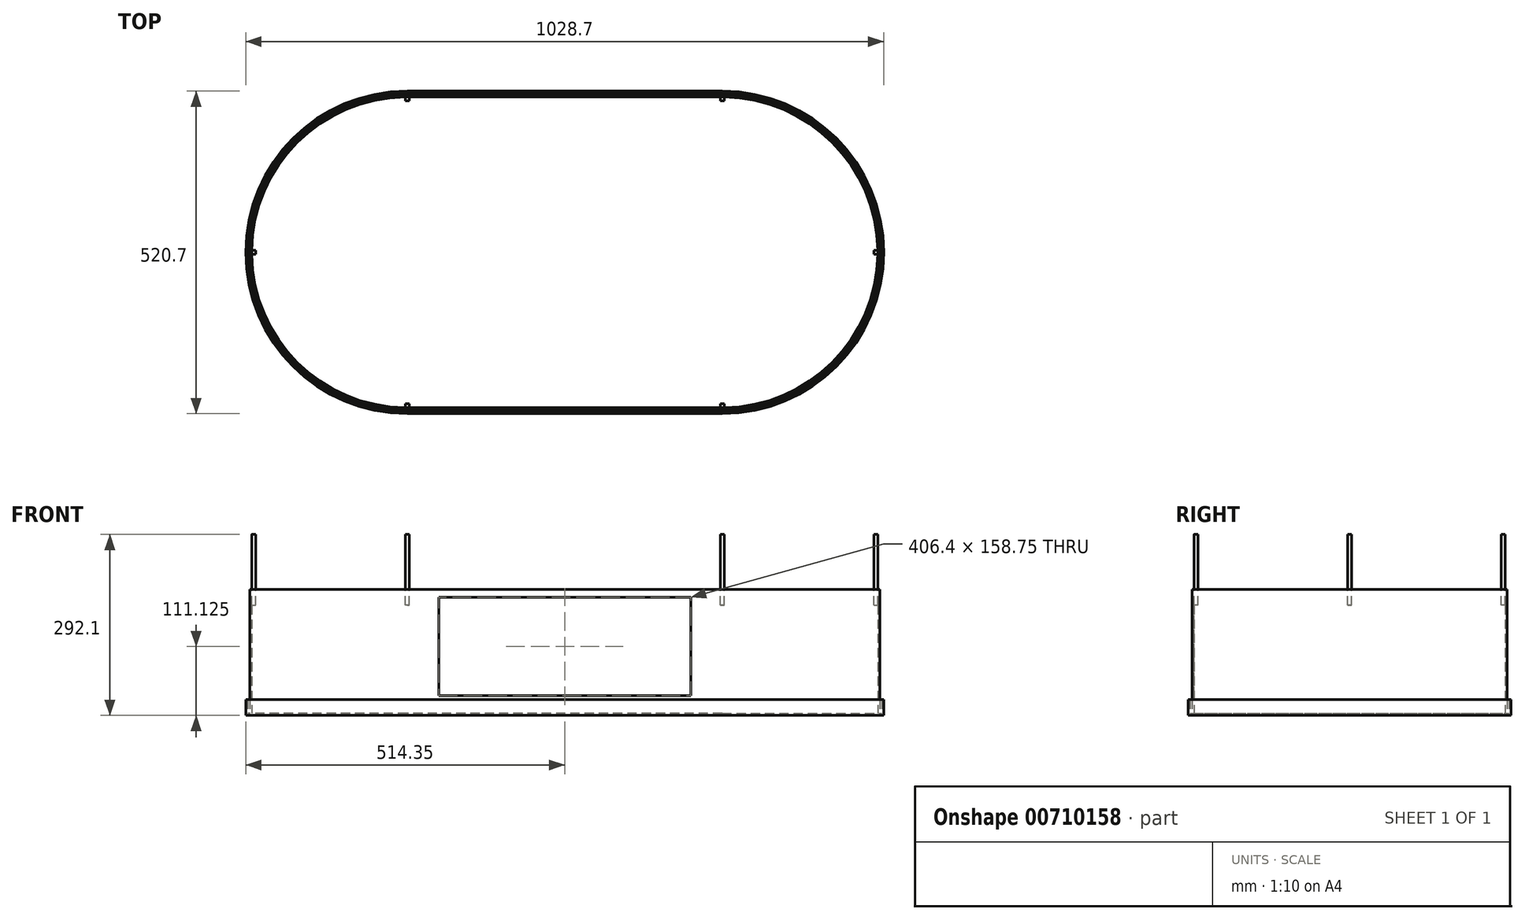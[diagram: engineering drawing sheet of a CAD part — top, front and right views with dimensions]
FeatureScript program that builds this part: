
annotation { "Feature Type Name" : "Feature", "Feature Type Description" : "" }
export const myFeature = defineFeature(function(context is Context, id is Id, definition is map)
    precondition{}
    {
        {
            var Q0;
            Q0=qCreatedBy(makeId("Top.planeOp"),FACE);
            var sketch = newSketch(context, id + "F0", { "sketchPlane" : qUnion([Q0])});
            skArc(sketch, "E0", {"start": v(0, -254) * mm, "mid": v(254, 0) * mm, "end": v(0, 254) * mm});
            skPoint(sketch, "E1.start.orphan", {"position": v(254, 0) * mm});
            skArc(sketch, "E2", {"start": v(-508, 254) * mm, "mid": v(-762, 0) * mm, "end": v(-508, -254) * mm});
            skLineSegment(sketch, "E3", {"start": v(0, 254) * mm, "end": v(-508, 254) * mm});
            skLineSegment(sketch, "E4", {"start": v(0, -254) * mm, "end": v(-508, -254) * mm});
            skSolve(sketch);
        }
        {
            var Q0;
            Q0=makeQuery(id+"F0.imprint","IMPRINT",FACE,{"disambiguationData":[TD([[makeQuery(id+"F0.imprint","IMPRINT",EDGE,{"derivedFrom":sQuery(id+"F0.wireOp",EDGE,"E0")}),1.0]])]});
            extrude(context, id + "F1", {"entities" : qUnion([Q0]), "depth" : 203.2 * mm, "offsetDistance" : 25.4 * mm});
        }
        {
            var Q0;
            Q0=makeQuery(id+"F1.opExtrude","CAP_FACE",FACE,{"disambiguationData":[OSD([sQuery(id+"F0.wireOp",EDGE,"E0"),sQuery(id+"F0.wireOp",EDGE,"sRwBP0qD-Oi6G-VSUF-o49D-kqOQtLQ9zoz9"),sQuery(id+"F0.wireOp",EDGE,"ZS3OsBiQ-hE2P-Jti2-7UnU-fXA1tlRt14Xo"),sQuery(id+"F0.wireOp",EDGE,"dp39ooyN-qIMO-7YCf-20ET-YGL1ctkYzJkL")])],"isStart":false});
            shell(context, id + "F2", {"entities" : qUnion([Q0]), "thickness" : 3.17 * mm});
        }
        {
            var Q0;
            Q0=makeQuery(id+"F1.opExtrude","SWEPT_FACE",FACE,{"disambiguationData":[OSD([sQuery(id+"F0.wireOp",EDGE,"E4")])]});
            cPlane(context, id + "F3", {"entities" : qUnion([Q0]), "cplaneType" : CPlaneType.OFFSET, "offset" : 0 * mm, "width" : 152.4 * mm, "height" : 152.4 * mm});
        }
        {
            var Q0;
            Q0=qCreatedBy(id+"F3.planeOp",FACE);
            var sketch = newSketch(context, id + "F4", { "sketchPlane" : qUnion([Q0])});
            skLineSegment(sketch, "E5.0.0", {"start": v(-508, 0) * mm, "end": v(0, 0) * mm});
            skLineSegment(sketch, "E5.0.1", {"start": v(0, 0) * mm, "end": v(0, 203.2) * mm});
            skLineSegment(sketch, "E5.0.2", {"start": v(0, 203.2) * mm, "end": v(-508, 203.2) * mm});
            skLineSegment(sketch, "E5.0.3", {"start": v(-508, 203.2) * mm, "end": v(-508, 0) * mm});
            skLineSegment(sketch, "E6.0", {"start": v(-50.8, 190.5) * mm, "end": v(-457.2, 190.5) * mm});
            skLineSegment(sketch, "E7.0", {"start": v(-457.2, 31.75) * mm, "end": v(-50.8, 31.75) * mm});
            skLineSegment(sketch, "E8.0", {"start": v(-50.8, 31.75) * mm, "end": v(-50.8, 190.5) * mm});
            skLineSegment(sketch, "E9.0", {"start": v(-457.2, 190.5) * mm, "end": v(-457.2, 31.75) * mm});
            skSolve(sketch);
        }
        {
            var Q0;
            Q0=makeQuery(id+"F4.imprint","IMPRINT",FACE,{"disambiguationData":[TD([[makeQuery(id+"F4.imprint","IMPRINT",EDGE,{"derivedFrom":sQuery(id+"F4.wireOp",EDGE,"E6.0")}),1.0]])]});
            extrude(context, id + "F5", {"entities" : qUnion([Q0]), "operationType" : NewBodyOperationType.REMOVE, "oppositeDirection" : true, "depth" : 25.4 * mm, "offsetDistance" : 25.4 * mm});
        }
        {
            var Q0;
            Q0=qCreatedBy(id+"F3.planeOp",FACE);
            var sketch = newSketch(context, id + "F6", { "sketchPlane" : qUnion([Q0])});
            skLineSegment(sketch, "E10.0", {"start": v(-50.8, 190.5) * mm, "end": v(-457.2, 190.5) * mm});
            skLineSegment(sketch, "E11.0", {"start": v(-457.2, 190.5) * mm, "end": v(-457.2, 31.75) * mm});
            skLineSegment(sketch, "E12.0", {"start": v(-457.2, 31.75) * mm, "end": v(-50.8, 31.75) * mm});
            skLineSegment(sketch, "E13.0", {"start": v(-50.8, 31.75) * mm, "end": v(-50.8, 190.5) * mm});
            skSolve(sketch);
        }
        {
            var Q0;
            Q0 = qSketchRegion(id + "F6", true);
            extrude(context, id + "F7", {"entities" : qUnion([Q0]), "oppositeDirection" : true, "depth" : 3.17 * mm, "offsetDistance" : 25.4 * mm});
        }
        {
            var Q0;
            Q0=makeQuery(id+"F1.opExtrude","CAP_FACE",FACE,{"disambiguationData":[OSD([sQuery(id+"F0.wireOp",EDGE,"E0"),sQuery(id+"F0.wireOp",EDGE,"E2"),sQuery(id+"F0.wireOp",EDGE,"E3"),sQuery(id+"F0.wireOp",EDGE,"E4")])],"isStart":true});
            cPlane(context, id + "F8", {"entities" : qUnion([Q0]), "cplaneType" : CPlaneType.OFFSET, "offset" : 0 * mm, "width" : 152.4 * mm, "height" : 152.4 * mm});
        }
        {
            var Q0;
            Q0=qCreatedBy(id+"F8.planeOp",FACE);
            var sketch = newSketch(context, id + "F9", { "sketchPlane" : qUnion([Q0])});
            skArc(sketch, "E14.0", {"start": v(-508, -260.35) * mm, "mid": v(-768.35, 0) * mm, "end": v(-508, 260.35) * mm});
            skLineSegment(sketch, "E14.1", {"start": v(0, -260.35) * mm, "end": v(-508, -260.35) * mm});
            skArc(sketch, "E14.2", {"start": v(0, 260.35) * mm, "mid": v(260.35, 0) * mm, "end": v(0, -260.35) * mm});
            skLineSegment(sketch, "E14.3", {"start": v(0, 260.35) * mm, "end": v(-508, 260.35) * mm});
            skSolve(sketch);
        }
        {
            var Q0;
            Q0 = qSketchRegion(id + "F9", true);
            extrude(context, id + "F10", {"entities" : qUnion([Q0]), "oppositeDirection" : true, "depth" : 25.4 * mm, "offsetDistance" : 25.4 * mm});
        }
        {
            var Q0;
            Q0=makeQuery(id+"F10.opExtrude","CAP_FACE",FACE,{"disambiguationData":[OSD([sQuery(id+"F9.wireOp",EDGE,"E14.0"),sQuery(id+"F9.wireOp",EDGE,"E14.1"),sQuery(id+"F9.wireOp",EDGE,"E14.2"),sQuery(id+"F9.wireOp",EDGE,"E14.3")])],"isStart":false});
            shell(context, id + "F11", {"entities" : qUnion([Q0]), "thickness" : 3.17 * mm});
        }
        {
            var Q0;
            Q0=makeQuery(id+"F1.opExtrude","CAP_FACE",FACE,{"disambiguationData":[OSD([sQuery(id+"F0.wireOp",EDGE,"E0"),sQuery(id+"F0.wireOp",EDGE,"E2"),sQuery(id+"F0.wireOp",EDGE,"E3"),sQuery(id+"F0.wireOp",EDGE,"E4")])],"isStart":false});
            cPlane(context, id + "F12", {"entities" : qUnion([Q0]), "cplaneType" : CPlaneType.OFFSET, "offset" : 0 * mm, "width" : 152.4 * mm, "height" : 152.4 * mm});
        }
        {
            var Q0;
            Q0=qCreatedBy(id+"F12.planeOp",FACE);
            var sketch = newSketch(context, id + "F13", { "sketchPlane" : qUnion([Q0])});
            skArc(sketch, "E15.0", {"start": v(-508, 250.83) * mm, "mid": v(-758.83, 0) * mm, "end": v(-508, -250.83) * mm});
            skLineSegment(sketch, "E16.0", {"start": v(0, 250.83) * mm, "end": v(-508, 250.83) * mm});
            skLineSegment(sketch, "E17.0.2", {"start": v(-508, -250.83) * mm, "end": v(0, -250.83) * mm});
            skArc(sketch, "E17.0.3", {"start": v(0, -250.83) * mm, "mid": v(250.83, 0) * mm, "end": v(0, 250.83) * mm});
            skLineSegment(sketch, "E18.0", {"start": v(-3.17, 250.83) * mm, "end": v(-3.17, 244.48) * mm});
            skLineSegment(sketch, "E19.0", {"start": v(3.18, 250.83) * mm, "end": v(3.18, 244.48) * mm});
            skLineSegment(sketch, "E20.0", {"start": v(-504.82, 250.83) * mm, "end": v(-504.82, 244.48) * mm});
            skLineSegment(sketch, "E21.0", {"start": v(-758.83, -3.18) * mm, "end": v(-752.48, -3.18) * mm});
            skLineSegment(sketch, "E22.0", {"start": v(-758.83, 3.17) * mm, "end": v(-752.48, 3.17) * mm});
            skLineSegment(sketch, "E23.0", {"start": v(-511.18, 250.83) * mm, "end": v(-511.18, 244.48) * mm});
            skLineSegment(sketch, "E24.0", {"start": v(0, 244.48) * mm, "end": v(-3.17, 244.48) * mm});
            skLineSegment(sketch, "E25.0", {"start": v(-508, -244.48) * mm, "end": v(-504.82, -244.48) * mm});
            skLineSegment(sketch, "E26", {"start": v(-508, -244.48) * mm, "end": v(-511.18, -244.48) * mm});
            skLineSegment(sketch, "E27", {"start": v(-508, 244.48) * mm, "end": v(-511.18, 244.48) * mm});
            skLineSegment(sketch, "E28", {"start": v(0, 244.48) * mm, "end": v(3.18, 244.48) * mm});
            skLineSegment(sketch, "E29", {"start": v(0, -244.48) * mm, "end": v(3.18, -244.48) * mm});
            skLineSegment(sketch, "E30.trimOffspring", {"start": v(-3.17, -244.48) * mm, "end": v(0, -244.48) * mm});
            skLineSegment(sketch, "E31.trimOffspring", {"start": v(-511.18, -244.48) * mm, "end": v(-511.18, -250.83) * mm});
            skLineSegment(sketch, "E32.trimOffspring", {"start": v(-504.82, -244.48) * mm, "end": v(-504.82, -250.83) * mm});
            skLineSegment(sketch, "E33", {"start": v(-752.48, 0) * mm, "end": v(-752.48, 3.17) * mm});
            skLineSegment(sketch, "E34", {"start": v(-752.48, 0) * mm, "end": v(-752.48, -3.18) * mm});
            skLineSegment(sketch, "E35", {"start": v(250.8, 3.18) * mm, "end": v(244.81, 3.18) * mm});
            skLineSegment(sketch, "E36", {"start": v(244.81, 3.18) * mm, "end": v(244.81, -3.17) * mm});
            skLineSegment(sketch, "E37.trimOffspring", {"start": v(244.81, -3.17) * mm, "end": v(250.83, -3.17) * mm});
            skLineSegment(sketch, "E38.trimOffspring", {"start": v(244.81, 3.18) * mm, "end": v(250.8, 3.18) * mm});
            skPoint(sketch, "E39.orphan", {"position": v(238.46, 3.18) * mm});
            skLineSegment(sketch, "E40.trimOffspring", {"start": v(3.18, -244.48) * mm, "end": v(3.18, -250.83) * mm});
            skLineSegment(sketch, "E41.trimOffspring", {"start": v(-3.17, -244.48) * mm, "end": v(-3.17, -250.83) * mm});
            skLineSegment(sketch, "E42.trimOffspring", {"start": v(-504.82, 244.48) * mm, "end": v(-508, 244.48) * mm});
            skPoint(sketch, "E43.start.orphan", {"position": v(-758.83, 0) * mm});
            skPoint(sketch, "E44.trimOffspring.end.orphan", {"position": v(250.83, 0) * mm});
            skPoint(sketch, "E45.orphan", {"position": v(251.16, 3.18) * mm});
            skSolve(sketch);
        }
        {
            var Q0;
            {var subQ4=sQuery(id+"F13.wireOp",EDGE,"E36");Q0=makeQuery(id+"F13.imprint","IMPRINT",FACE,{"disambiguationData":[TD([[makeQuery(id+"F13.imprint","IMPRINT",EDGE,{"derivedFrom":subQ4}),1.0]])]});}
            var Q1;
            {var subQ4=sQuery(id+"F13.wireOp",EDGE,"E18.0");Q1=makeQuery(id+"F13.imprint","IMPRINT",FACE,{"disambiguationData":[TD([[makeQuery(id+"F13.imprint","IMPRINT",EDGE,{"derivedFrom":subQ4}),1.0]])]});}
            var Q2;
            {var subQ4=sQuery(id+"F13.wireOp",EDGE,"E20.0");Q2=makeQuery(id+"F13.imprint","IMPRINT",FACE,{"disambiguationData":[TD([[makeQuery(id+"F13.imprint","IMPRINT",EDGE,{"derivedFrom":subQ4}),-1.0]])]});}
            var Q3;
            {var subQ0=sQuery(id+"F13.wireOp",EDGE,"E33");Q3=makeQuery(id+"F13.imprint","IMPRINT",FACE,{"disambiguationData":[TD([[makeQuery(id+"F13.imprint","IMPRINT",EDGE,{"derivedFrom":subQ0}),1.0]])]});}
            var Q4;
            Q4=makeQuery(id+"F13.imprint","IMPRINT",FACE,{"disambiguationData":[TD([[makeQuery(id+"F13.imprint","IMPRINT",EDGE,{"derivedFrom":sQuery(id+"F13.wireOp",EDGE,"E25.0")}),-1.0]])]});
            var Q5;
            {var subQ0=sQuery(id+"F13.wireOp",EDGE,"E29");Q5=makeQuery(id+"F13.imprint","IMPRINT",FACE,{"disambiguationData":[TD([[makeQuery(id+"F13.imprint","IMPRINT",EDGE,{"derivedFrom":subQ0}),-1.0]])]});}
            extrude(context, id + "F14", {"entities" : qUnion([Q0, Q1, Q2, Q3, Q4, Q5]), "operationType" : NewBodyOperationType.ADD, "oppositeDirection" : true, "depth" : 25.4 * mm, "offsetDistance" : 25.4 * mm, "hasSecondDirection" : true, "secondDirectionOppositeDirection" : false, "secondDirectionDepth" : 88.9 * mm});
        }
    });
